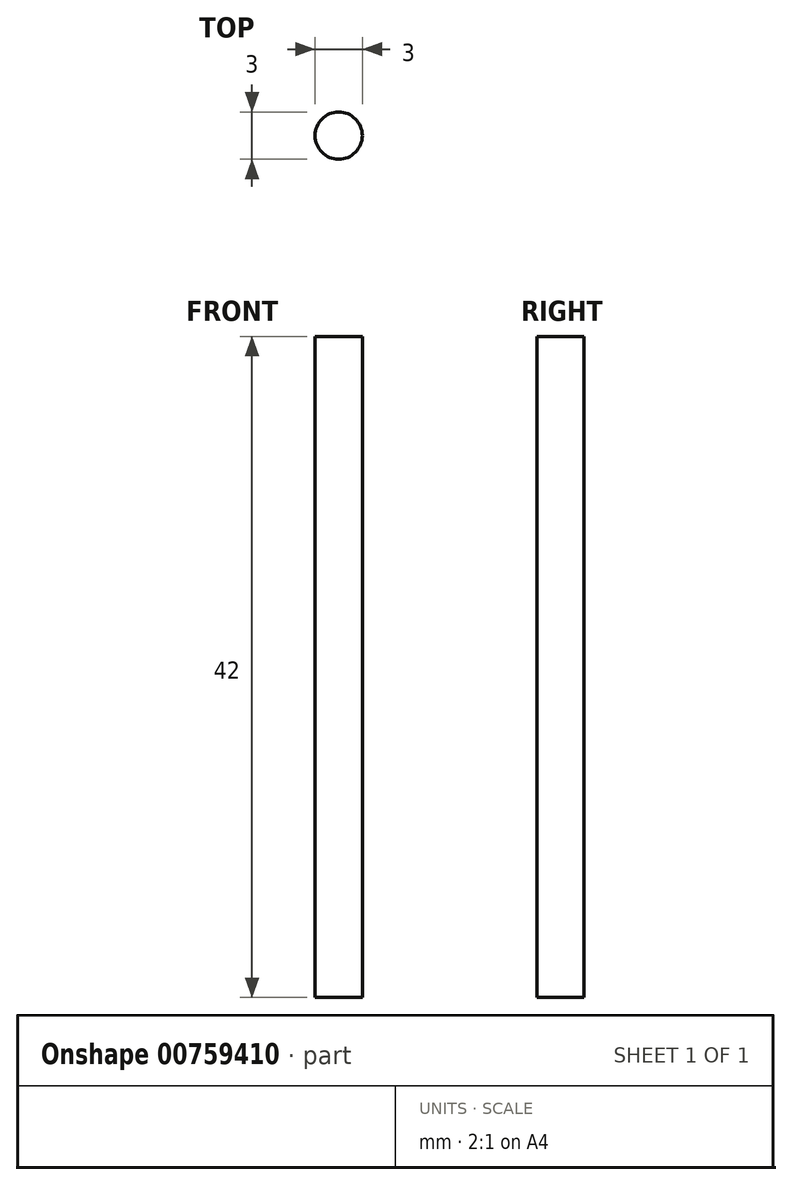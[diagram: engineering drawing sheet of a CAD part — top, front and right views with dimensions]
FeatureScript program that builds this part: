
annotation { "Feature Type Name" : "Feature", "Feature Type Description" : "" }
export const myFeature = defineFeature(function(context is Context, id is Id, definition is map)
    precondition{}
    {
        {
            var Q0;
            Q0=qCreatedBy(makeId("Top.planeOp"),FACE);
            var sketch = newSketch(context, id + "F0", { "sketchPlane" : qUnion([Q0])});
            skCircle(sketch, "E0", {"center": v(0, 0) * mm, "radius": 1.5 * mm});
            skSolve(sketch);
        }
        {
            var Q0;
            Q0 = qSketchRegion(id + "F0", true);
            extrude(context, id + "F1", {"entities" : qUnion([Q0]), "endBound" : BoundingType.SYMMETRIC, "depth" : 42 * mm, "offsetDistance" : 25 * mm});
        }
    });
